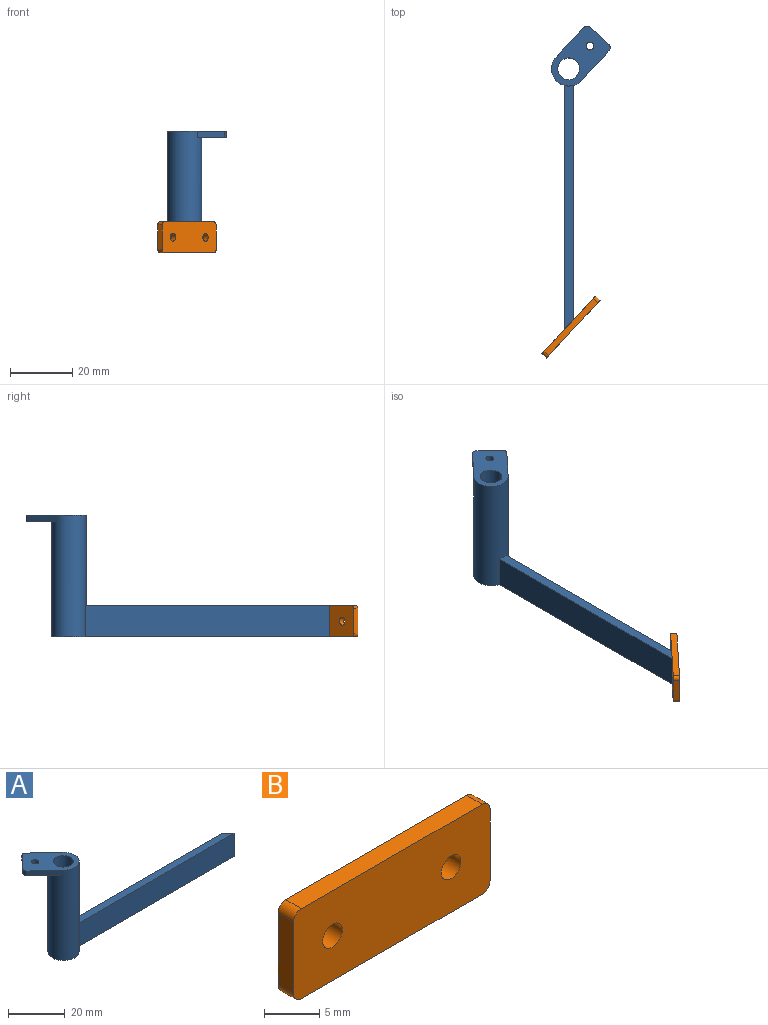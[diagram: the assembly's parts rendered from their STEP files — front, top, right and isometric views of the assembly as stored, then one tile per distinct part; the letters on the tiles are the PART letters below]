
ASSEMBLY  parts=2 mates=1
PART A: 15 faces, bbox 97.3x18.8x39 mm
  f0: plane 89.09x11mm, normal (0,0,-1), area 286.2mm2, adj f1,f2,f3,f4,f6
  f1: cylinder r=5.5mm len=39mm, axis (0,0,-1), area 1282.8mm2, adj f0,f2,f3,f5,f7,f8,f13,f14
  f2: plane 75.08x10mm, normal (0,1,0), area 750.8mm2, adj f0,f1,f4,f5
  f3: plane 78.3x10mm, normal (0,-1,0), area 783mm2, adj f0,f1,f4,f5
  f4: plane 10x3.22mm, normal (0.68,0.73,0), area 44mm2, adj f0,f2,f3,f5
  f5: plane 78.3x3mm, normal (0,0,1), area 229.7mm2, adj f1,f2,f3,f4
  f6: cylinder r=3.5mm len=39mm, axis (0,0,-1), area 857.7mm2, adj f0,f7
  f7: plane 19.24x18.79mm, normal (0,0,1), area 162.5mm2, adj f1,f6,f8,f9,f10,f11,f12,f13
  f8: plane 9.51x8.87mm, normal (0.68,0.73,0), area 26mm2, adj f1,f7,f9,f14
  f9: cylinder r=1.5mm len=2.12mm, axis (0,0,-1), area 4.7mm2, adj f7,f8,f10,f14
  f10: plane 5.85x5.46mm, normal (-0.73,0.68,0), area 16mm2, adj f7,f9,f11,f14
  f11: cylinder r=1.5mm len=2.12mm, axis (0,0,-1), area 4.7mm2, adj f7,f10,f13,f14
  f12: cylinder r=1.27mm len=2.54mm, axis (0,0,-1), area 16mm2, adj f7,f14
  f13: plane 9.51x8.87mm, normal (-0.68,-0.73,0), area 26mm2, adj f1,f7,f11,f14
  f14: plane 17.49x17.31mm, normal (0,0,-1), area 106mm2, adj f1,f8,f9,f10,f11,f12,f13
PART B: 12 faces, bbox 25.2x2x10 mm
  f0: cylinder r=1mm len=2mm, axis (0,1,0), area 3.1mm2, adj f1,f9,f10,f11
  f1: plane 23.24x2mm, normal (0,0,-1), area 46.5mm2, adj f0,f2,f10,f11
  f2: cylinder r=1mm len=2mm, axis (0,1,0), area 3.1mm2, adj f1,f3,f10,f11
  f3: plane 8x2mm, normal (1,0,0), area 16mm2, adj f2,f4,f10,f11
  f4: cylinder r=1mm len=2mm, axis (0,1,0), area 3.1mm2, adj f3,f5,f10,f11
  f5: plane 23.24x2mm, normal (0,0,1), area 46.5mm2, adj f4,f6,f10,f11
  f6: cylinder r=1mm len=2mm, axis (0,1,0), area 3.1mm2, adj f5,f9,f10,f11
  f7: cylinder r=1.27mm len=2.54mm, axis (0,1,0), area 16mm2, adj f10,f11
  f8: cylinder r=1.27mm len=2.54mm, axis (0,1,0), area 16mm2, adj f10,f11
  f9: plane 8x2mm, normal (-1,0,0), area 16mm2, adj f0,f6,f10,f11
  f10: plane 25.24x10mm, normal (0,-1,0), area 241.4mm2, adj f0,f1,f2,f3,f4,f5,f6,f7
  f11: plane 25.24x10mm, normal (0,1,0), area 241.4mm2, adj f0,f1,f2,f3,f4,f5,f6,f7
PLACE A rot(axis=(0,0,-1),90deg) t=(0.01,-9.42,0)mm
PLACE B rot(axis=(0,0,1),47deg) t=(5.02,-41.54,2.05)mm
MATE fastened A.f4 <-> B.f11  axis (0.73,-0.68,0) through (0.01,-46.91,5)mm
